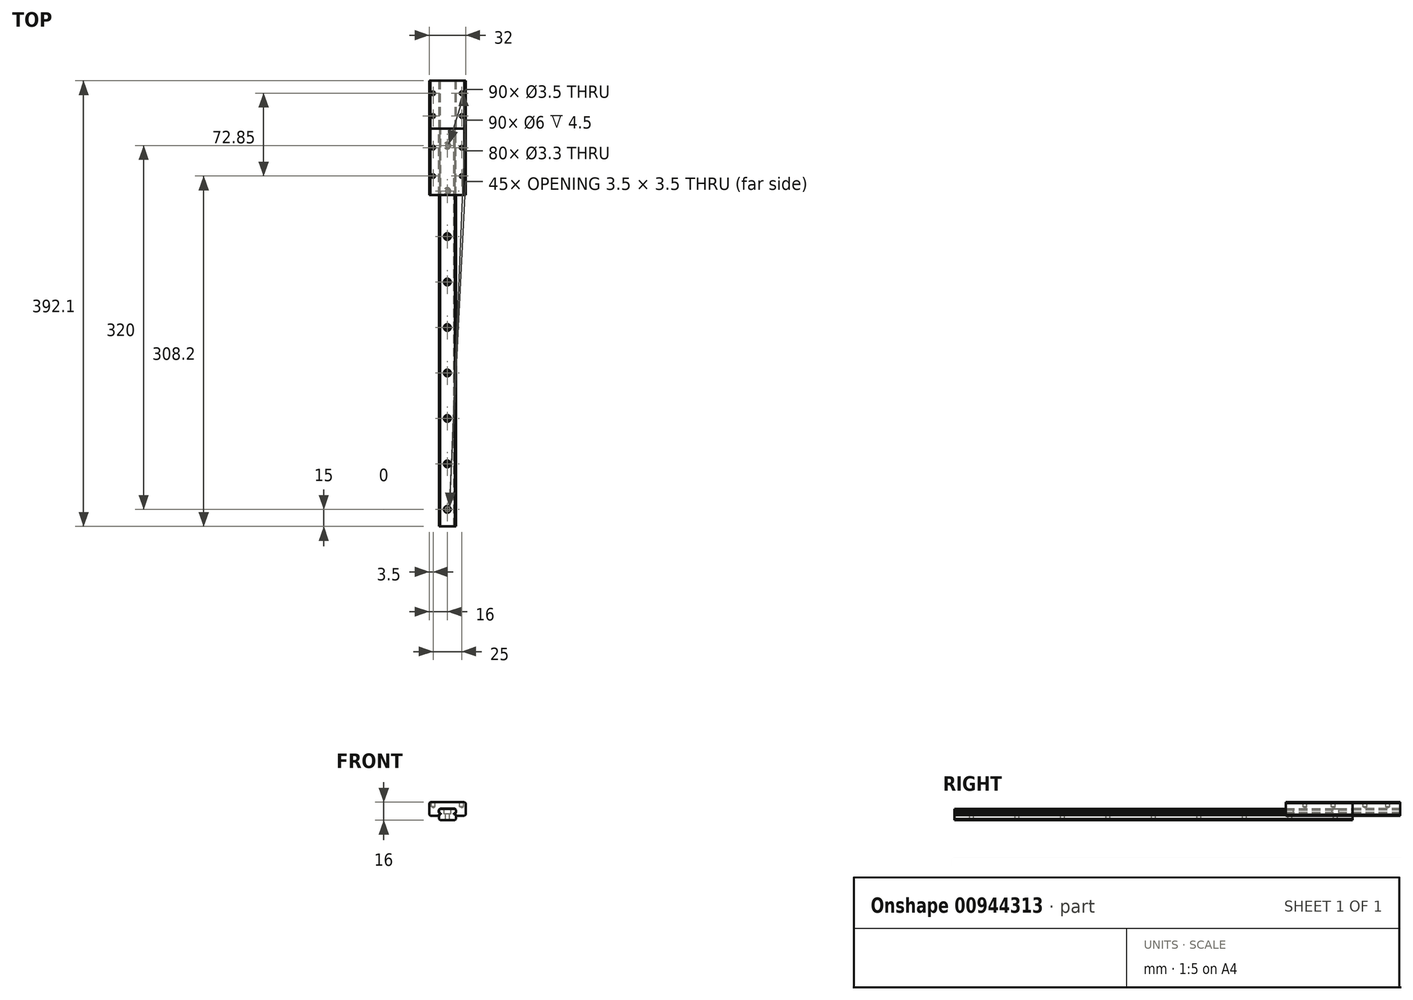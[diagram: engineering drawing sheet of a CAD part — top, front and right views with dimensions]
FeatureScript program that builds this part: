
annotation { "Feature Type Name" : "Feature", "Feature Type Description" : "" }
export const myFeature = defineFeature(function(context is Context, id is Id, definition is map)
    precondition{}
    {
        {
            var Q0;
            Q0=qCreatedBy(makeId("Front.planeOp"),FACE);
            var sketch = newSketch(context, id + "F0", { "sketchPlane" : qUnion([Q0])});
            skLineSegment(sketch, "E0.bottom", {"start": v(6.5, -5) * mm, "end": v(-6.5, -5) * mm});
            skLineSegment(sketch, "E0.top", {"start": v(6.5, 5) * mm, "end": v(-6.5, 5) * mm});
            skLineSegment(sketch, "E0.left", {"start": v(7.5, -4) * mm, "end": v(7.5, -0.41) * mm});
            skLineSegment(sketch, "E0.right", {"start": v(-7.5, -4) * mm, "end": v(-7.5, -0.41) * mm});
            skPoint(sketch, "E0.middle", {"position": v(0, 0) * mm});
            skLineSegment(sketch, "E1", {"start": v(0, 12.36) * mm, "end": v(0, -9.73) * mm, "construction": true});
            skLineSegment(sketch, "E2", {"start": v(-7.5, 2) * mm, "end": v(-6.8, 1.3) * mm});
            skLineSegment(sketch, "E3", {"start": v(-6.8, 1.3) * mm, "end": v(-5.8, 1.3) * mm});
            skLineSegment(sketch, "E4", {"start": v(-5.8, 1.3) * mm, "end": v(-5.8, 0.3) * mm});
            skLineSegment(sketch, "E5", {"start": v(-5.8, 0.3) * mm, "end": v(-6.8, 0.3) * mm});
            skLineSegment(sketch, "E6", {"start": v(-6.8, 0.3) * mm, "end": v(-7.5, -0.41) * mm});
            skLineSegment(sketch, "E7.MirrorCS", {"start": v(5.8, 0.3) * mm, "end": v(6.8, 0.3) * mm});
            skLineSegment(sketch, "E8.MirrorCS", {"start": v(6.8, 0.3) * mm, "end": v(7.5, -0.41) * mm});
            skLineSegment(sketch, "E9.MirrorCS", {"start": v(5.8, 1.3) * mm, "end": v(5.8, 0.3) * mm});
            skLineSegment(sketch, "E10.MirrorCS", {"start": v(7.5, 2) * mm, "end": v(6.8, 1.3) * mm});
            skLineSegment(sketch, "E11.MirrorCS", {"start": v(6.8, 1.3) * mm, "end": v(5.8, 1.3) * mm});
            skLineSegment(sketch, "E12.trimOffspring", {"start": v(-7.5, 2) * mm, "end": v(-7.5, 4) * mm});
            skLineSegment(sketch, "E13.trimOffspring", {"start": v(7.5, 2) * mm, "end": v(7.5, 4) * mm});
            skLineSegment(sketch, "E14", {"start": v(-7.5, 4) * mm, "end": v(-6.5, 5) * mm});
            skLineSegment(sketch, "E15.MirrorCS", {"start": v(7.5, 4) * mm, "end": v(6.5, 5) * mm});
            skLineSegment(sketch, "E16.MirrorCS", {"start": v(-7.5, -4) * mm, "end": v(-6.5, -5) * mm});
            skLineSegment(sketch, "E17.MirrorCS", {"start": v(7.5, -4) * mm, "end": v(6.5, -5) * mm});
            skPoint(sketch, "E18.orphan", {"position": v(-7.5, 5) * mm});
            skPoint(sketch, "E19.orphan", {"position": v(7.5, 5) * mm});
            skPoint(sketch, "E20.orphan", {"position": v(7.5, -5) * mm});
            skPoint(sketch, "E21.orphan", {"position": v(-7.5, -5) * mm});
            skSolve(sketch);
        }
        {
            var Q0;
            Q0=makeQuery(id+"F0.imprint","IMPRINT",FACE,{"disambiguationData":[TD([[makeQuery(id+"F0.imprint","IMPRINT",EDGE,{"derivedFrom":sQuery(id+"F0.wireOp",EDGE,"E0.bottom")}),-1.0]])]});
            extrude(context, id + "F1", {"entities" : qUnion([Q0]), "depth" : 350 * mm, "offsetDistance" : 25 * mm});
        }
        {
            var Q0;
            Q0=makeQuery(id+"F1.opExtrude","SWEPT_FACE",FACE,{"disambiguationData":[OSD([sQuery(id+"F0.wireOp",EDGE,"E0.top")])]});
            var sketch = newSketch(context, id + "F2", { "sketchPlane" : qUnion([Q0])});
            skLineSegment(sketch, "E22", {"start": v(0, 4.61) * mm, "end": v(0, -375.08) * mm, "construction": true});
            skCircle(sketch, "E23", {"center": v(0, -15) * mm, "radius": 1.75 * mm});
            skCircle(sketch, "E24.1.0.0", {"center": v(0, -55) * mm, "radius": 1.75 * mm});
            skCircle(sketch, "E24.2.0.0", {"center": v(0, -95) * mm, "radius": 1.75 * mm});
            skCircle(sketch, "E24.3.0.0", {"center": v(0, -135) * mm, "radius": 1.75 * mm});
            skCircle(sketch, "E24.4.0.0", {"center": v(0, -175) * mm, "radius": 1.75 * mm});
            skCircle(sketch, "E24.5.0.0", {"center": v(0, -215) * mm, "radius": 1.75 * mm});
            skCircle(sketch, "E24.6.0.0", {"center": v(0, -255) * mm, "radius": 1.75 * mm});
            skCircle(sketch, "E24.7.0.0", {"center": v(0, -295) * mm, "radius": 1.75 * mm});
            skCircle(sketch, "E24.8.0.0", {"center": v(0, -335) * mm, "radius": 1.75 * mm});
            skLineSegment(sketch, "E24.direction1", {"start": v(0, -15) * mm, "end": v(0, -55) * mm, "construction": true});
            skSolve(sketch);
        }
        {
            var Q0;
            Q0=qSketchRegion(id+"F2",true);
            extrude(context, id + "F3", {"entities" : qUnion([Q0]), "operationType" : NewBodyOperationType.REMOVE, "endBound" : BoundingType.THROUGH_ALL, "oppositeDirection" : true, "depth" : 25 * mm, "offsetDistance" : 25 * mm});
        }
        {
            var Q0;
            Q0=makeQuery(id+"F1.opExtrude","SWEPT_FACE",FACE,{"disambiguationData":[OSD([sQuery(id+"F0.wireOp",EDGE,"E0.top")])]});
            var sketch = newSketch(context, id + "F4", { "sketchPlane" : qUnion([Q0])});
            skLineSegment(sketch, "E25", {"start": v(0, 167.82) * mm, "end": v(0, -211.88) * mm, "construction": true});
            skCircle(sketch, "E26", {"center": v(0, -15) * mm, "radius": 3 * mm});
            skCircle(sketch, "E27.1.0.0", {"center": v(0, -55) * mm, "radius": 3 * mm});
            skCircle(sketch, "E27.2.0.0", {"center": v(0, -95) * mm, "radius": 3 * mm});
            skCircle(sketch, "E27.3.0.0", {"center": v(0, -135) * mm, "radius": 3 * mm});
            skCircle(sketch, "E27.4.0.0", {"center": v(0, -175) * mm, "radius": 3 * mm});
            skCircle(sketch, "E27.5.0.0", {"center": v(0, -215) * mm, "radius": 3 * mm});
            skCircle(sketch, "E27.6.0.0", {"center": v(0, -255) * mm, "radius": 3 * mm});
            skCircle(sketch, "E27.7.0.0", {"center": v(0, -295) * mm, "radius": 3 * mm});
            skCircle(sketch, "E27.8.0.0", {"center": v(0, -335) * mm, "radius": 3 * mm});
            skLineSegment(sketch, "E27.direction1", {"start": v(0, -15) * mm, "end": v(0, -55) * mm, "construction": true});
            skSolve(sketch);
        }
        {
            var Q0;
            Q0=qSketchRegion(id+"F4",true);
            extrude(context, id + "F5", {"entities" : qUnion([Q0]), "operationType" : NewBodyOperationType.REMOVE, "oppositeDirection" : true, "depth" : 4.5 * mm, "offsetDistance" : 25 * mm});
        }
        {
            var Q0;
            Q0=qCreatedBy(makeId("Front.planeOp"),FACE);
            var sketch = newSketch(context, id + "F6", { "sketchPlane" : qUnion([Q0])});
            skLineSegment(sketch, "E28", {"start": v(-7.65, -1) * mm, "end": v(-15, -1) * mm});
            skLineSegment(sketch, "E29", {"start": v(-16, 0) * mm, "end": v(-16, 10) * mm});
            skLineSegment(sketch, "E30", {"start": v(-15, 11) * mm, "end": v(0, 11) * mm});
            skLineSegment(sketch, "E31", {"start": v(-7.65, -1) * mm, "end": v(-7.65, -0.35) * mm});
            skLineSegment(sketch, "E32", {"start": v(-7.65, -0.35) * mm, "end": v(-6.8, 0.5) * mm});
            skLineSegment(sketch, "E33", {"start": v(-6.8, 0.5) * mm, "end": v(-6.8, 1.08) * mm});
            skLineSegment(sketch, "E34", {"start": v(-6.8, 1.08) * mm, "end": v(-7.65, 1.94) * mm});
            skLineSegment(sketch, "E35", {"start": v(-7.65, 1.94) * mm, "end": v(-7.65, 4.06) * mm});
            skLineSegment(sketch, "E36", {"start": v(-7.65, 4.06) * mm, "end": v(-6.56, 5.15) * mm});
            skLineSegment(sketch, "E37", {"start": v(-6.56, 5.15) * mm, "end": v(0, 5.15) * mm});
            skLineSegment(sketch, "E38", {"start": v(-16, 10) * mm, "end": v(-15, 11) * mm});
            skLineSegment(sketch, "E39", {"start": v(-15, -1) * mm, "end": v(-16, 0) * mm});
            skPoint(sketch, "E40.orphan", {"position": v(-16, -1) * mm});
            skPoint(sketch, "E41.orphan", {"position": v(-16, 11) * mm});
            skLineSegment(sketch, "E42.MirrorCS", {"start": v(15, 11) * mm, "end": v(0, 11) * mm});
            skLineSegment(sketch, "E43.MirrorCS", {"start": v(16, 10) * mm, "end": v(15, 11) * mm});
            skLineSegment(sketch, "E44.MirrorCS", {"start": v(16, 0) * mm, "end": v(16, 10) * mm});
            skLineSegment(sketch, "E45.MirrorCS", {"start": v(15, -1) * mm, "end": v(16, 0) * mm});
            skLineSegment(sketch, "E46.MirrorCS", {"start": v(7.65, -1) * mm, "end": v(15, -1) * mm});
            skLineSegment(sketch, "E47.MirrorCS", {"start": v(7.65, -1) * mm, "end": v(7.65, -0.35) * mm});
            skLineSegment(sketch, "E48.MirrorCS", {"start": v(7.65, -0.35) * mm, "end": v(6.8, 0.5) * mm});
            skLineSegment(sketch, "E49.MirrorCS", {"start": v(6.8, 0.5) * mm, "end": v(6.8, 1.08) * mm});
            skLineSegment(sketch, "E50.MirrorCS", {"start": v(6.8, 1.08) * mm, "end": v(7.65, 1.94) * mm});
            skLineSegment(sketch, "E51.MirrorCS", {"start": v(7.65, 1.94) * mm, "end": v(7.65, 4.06) * mm});
            skLineSegment(sketch, "E52.MirrorCS", {"start": v(7.65, 4.06) * mm, "end": v(6.56, 5.15) * mm});
            skLineSegment(sketch, "E53.MirrorCS", {"start": v(6.56, 5.15) * mm, "end": v(0, 5.15) * mm});
            skSolve(sketch);
        }
        {
            var Q0;
            Q0=qSketchRegion(id+"F6",true);
            extrude(context, id + "F7", {"entities" : qUnion([Q0]), "depth" : 58.6 * mm, "offsetDistance" : 25 * mm});
        }
        {
            var Q0;
            Q0=qSketchRegion(id+"F6",true);
            extrude(context, id + "F8", {"entities" : qUnion([Q0]), "oppositeDirection" : true, "depth" : 42.1 * mm, "offsetDistance" : 25 * mm});
        }
        {
            var Q0;
            Q0=makeQuery(id+"F7.opExtrude","SWEPT_FACE",FACE,{"disambiguationData":[OSD([sQuery(id+"F6.wireOp",EDGE,"E30"),sQuery(id+"F6.wireOp",EDGE,"E42.MirrorCS")])]});
            var sketch = newSketch(context, id + "F9", { "sketchPlane" : qUnion([Q0])});
            skLineSegment(sketch, "E54", {"start": v(-15, 0) * mm, "end": v(15, -58.6) * mm, "construction": true});
            skLineSegment(sketch, "E55", {"start": v(15, 0) * mm, "end": v(-15, -58.6) * mm, "construction": true});
            skLineSegment(sketch, "E56", {"start": v(-37.81, -29.3) * mm, "end": v(32.35, -29.3) * mm, "construction": true});
            skPoint(sketch, "E56.startSnap0", {"position": v(0, -29.3) * mm});
            skLineSegment(sketch, "E57", {"start": v(0, 0) * mm, "end": v(0, -61.52) * mm, "construction": true});
            skCircle(sketch, "E58", {"center": v(-12.5, -16.8) * mm, "radius": 1.5 * mm});
            skCircle(sketch, "E59.MirrorC", {"center": v(12.5, -16.8) * mm, "radius": 1.5 * mm});
            skCircle(sketch, "E60.MirrorC", {"center": v(-12.5, -41.8) * mm, "radius": 1.5 * mm});
            skCircle(sketch, "E61.MirrorC", {"center": v(12.5, -41.8) * mm, "radius": 1.5 * mm});
            skSolve(sketch);
        }
        {
            var Q0;
            Q0=makeQuery(id+"F8.opExtrude","SWEPT_FACE",FACE,{"disambiguationData":[OSD([sQuery(id+"F6.wireOp",EDGE,"E30"),sQuery(id+"F6.wireOp",EDGE,"E42.MirrorCS")])]});
            var sketch = newSketch(context, id + "F10", { "sketchPlane" : qUnion([Q0])});
            skLineSegment(sketch, "E62", {"start": v(-34.35, 21.05) * mm, "end": v(28.23, 21.05) * mm, "construction": true});
            skLineSegment(sketch, "E63", {"start": v(0, 49.38) * mm, "end": v(0, -1.77) * mm, "construction": true});
            skCircle(sketch, "E64", {"center": v(-12.5, 31.05) * mm, "radius": 1.5 * mm});
            skCircle(sketch, "E65.MirrorC", {"center": v(12.5, 31.05) * mm, "radius": 1.5 * mm});
            skCircle(sketch, "E66.MirrorC", {"center": v(-12.5, 11.05) * mm, "radius": 1.5 * mm});
            skCircle(sketch, "E67.MirrorC", {"center": v(12.5, 11.05) * mm, "radius": 1.5 * mm});
            skSolve(sketch);
        }
        {
            var Q0;
            Q0=sQuery(id+"F9.wireOp",VERTEX,"E58.center");
            var Q1;
            Q1=sQuery(id+"F9.wireOp",VERTEX,"E59.MirrorC.center");
            var Q2;
            Q2=sQuery(id+"F9.wireOp",VERTEX,"E60.MirrorC.center");
            var Q3;
            Q3=sQuery(id+"F9.wireOp",VERTEX,"E61.MirrorC.center");
            var Q4;
            Q4=makeQuery(id+"F7.opExtrude","SWEPT_BODY",BODY,{"disambiguationData":[OSD([sQuery(id+"F6.wireOp",EDGE,"E28"),sQuery(id+"F6.wireOp",EDGE,"E29"),sQuery(id+"F6.wireOp",EDGE,"E30"),sQuery(id+"F6.wireOp",EDGE,"E31"),sQuery(id+"F6.wireOp",EDGE,"E32"),sQuery(id+"F6.wireOp",EDGE,"E33"),sQuery(id+"F6.wireOp",EDGE,"E34"),sQuery(id+"F6.wireOp",EDGE,"E35"),sQuery(id+"F6.wireOp",EDGE,"E36"),sQuery(id+"F6.wireOp",EDGE,"E37"),sQuery(id+"F6.wireOp",EDGE,"E38"),sQuery(id+"F6.wireOp",EDGE,"E39"),sQuery(id+"F6.wireOp",EDGE,"E42.MirrorCS"),sQuery(id+"F6.wireOp",EDGE,"E43.MirrorCS"),sQuery(id+"F6.wireOp",EDGE,"E44.MirrorCS"),sQuery(id+"F6.wireOp",EDGE,"E45.MirrorCS"),sQuery(id+"F6.wireOp",EDGE,"E46.MirrorCS"),sQuery(id+"F6.wireOp",EDGE,"E47.MirrorCS"),sQuery(id+"F6.wireOp",EDGE,"E48.MirrorCS"),sQuery(id+"F6.wireOp",EDGE,"E49.MirrorCS"),sQuery(id+"F6.wireOp",EDGE,"E50.MirrorCS"),sQuery(id+"F6.wireOp",EDGE,"E51.MirrorCS"),sQuery(id+"F6.wireOp",EDGE,"E52.MirrorCS"),sQuery(id+"F6.wireOp",EDGE,"E53.MirrorCS")])]});
            hole(context, id + "F11", {"style" : HoleStyle.SIMPLE, "endStyle" : HoleEndStyle.BLIND, "standardTappedOrClearance" : lookupTablePath({ "standard" : "ISO", "fit" : "Normal", "size" : "M3", "type" : "Clearance" }), "standardBlindInLast" : lookupTablePath({ "fit" : "Standard", "standard" : "ISO", "size" : "M3", "type" : "Clearance" }), "holeDiameter" : 3.3 * mm, "majorDiameter" : 5 * mm, "holeDepth" : 4 * mm, "isTappedThrough" : true, "tappedDepth" : 12 * mm, "tapClearance" : 3, "startFromSketch" : true, "locations" : qUnion([Q0, Q1, Q2, Q3]), "scope" : qUnion([Q4])});
        }
        {
            var Q0;
            Q0=sQuery(id+"F10.wireOp",VERTEX,"E64.center");
            var Q1;
            Q1=sQuery(id+"F10.wireOp",VERTEX,"E65.MirrorC.center");
            var Q2;
            Q2=sQuery(id+"F10.wireOp",VERTEX,"E67.MirrorC.center");
            var Q3;
            Q3=sQuery(id+"F10.wireOp",VERTEX,"E66.MirrorC.center");
            var Q4;
            Q4=makeQuery(id+"F8.opExtrude","SWEPT_BODY",BODY,{"disambiguationData":[OSD([sQuery(id+"F6.wireOp",EDGE,"E28"),sQuery(id+"F6.wireOp",EDGE,"E29"),sQuery(id+"F6.wireOp",EDGE,"E30"),sQuery(id+"F6.wireOp",EDGE,"E31"),sQuery(id+"F6.wireOp",EDGE,"E32"),sQuery(id+"F6.wireOp",EDGE,"E33"),sQuery(id+"F6.wireOp",EDGE,"E34"),sQuery(id+"F6.wireOp",EDGE,"E35"),sQuery(id+"F6.wireOp",EDGE,"E36"),sQuery(id+"F6.wireOp",EDGE,"E37"),sQuery(id+"F6.wireOp",EDGE,"E38"),sQuery(id+"F6.wireOp",EDGE,"E39"),sQuery(id+"F6.wireOp",EDGE,"E42.MirrorCS"),sQuery(id+"F6.wireOp",EDGE,"E43.MirrorCS"),sQuery(id+"F6.wireOp",EDGE,"E44.MirrorCS"),sQuery(id+"F6.wireOp",EDGE,"E45.MirrorCS"),sQuery(id+"F6.wireOp",EDGE,"E46.MirrorCS"),sQuery(id+"F6.wireOp",EDGE,"E47.MirrorCS"),sQuery(id+"F6.wireOp",EDGE,"E48.MirrorCS"),sQuery(id+"F6.wireOp",EDGE,"E49.MirrorCS"),sQuery(id+"F6.wireOp",EDGE,"E50.MirrorCS"),sQuery(id+"F6.wireOp",EDGE,"E51.MirrorCS"),sQuery(id+"F6.wireOp",EDGE,"E52.MirrorCS"),sQuery(id+"F6.wireOp",EDGE,"E53.MirrorCS")])]});
            hole(context, id + "F12", {"style" : HoleStyle.SIMPLE, "endStyle" : HoleEndStyle.BLIND, "standardTappedOrClearance" : lookupTablePath({ "standard" : "ISO", "fit" : "Normal", "size" : "M3", "type" : "Clearance" }), "standardBlindInLast" : lookupTablePath({ "fit" : "Standard", "standard" : "ISO", "size" : "M3", "type" : "Clearance" }), "holeDiameter" : 3.3 * mm, "majorDiameter" : 5 * mm, "holeDepth" : 4 * mm, "isTappedThrough" : true, "tappedDepth" : 12 * mm, "tapClearance" : 3, "startFromSketch" : true, "locations" : qUnion([Q0, Q1, Q2, Q3]), "scope" : qUnion([Q4])});
        }
    });
